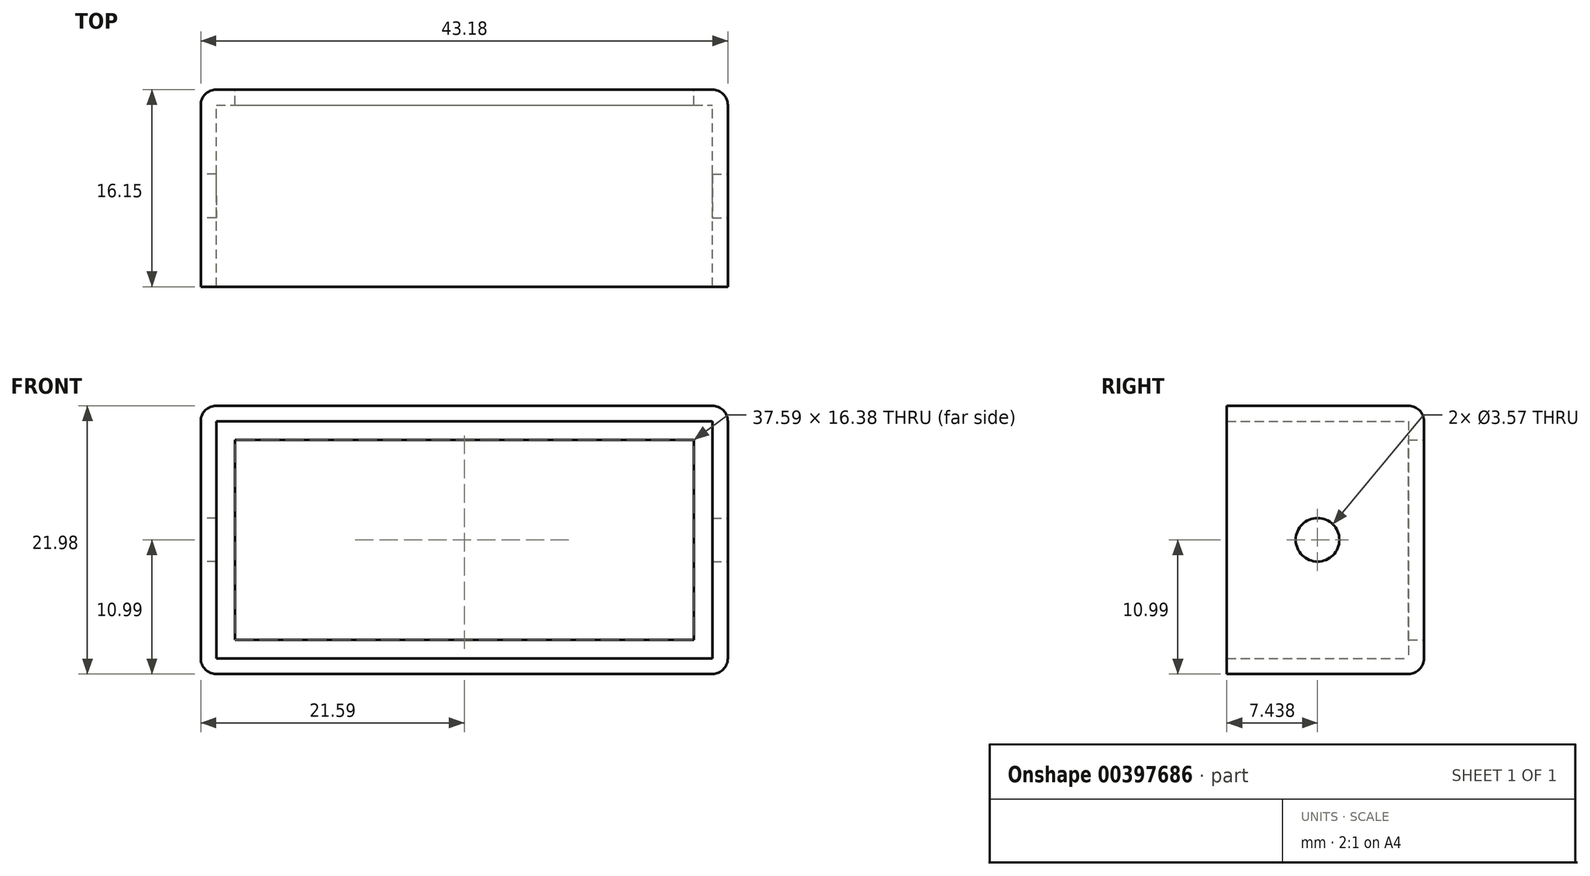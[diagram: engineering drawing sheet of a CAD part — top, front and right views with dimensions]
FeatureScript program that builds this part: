
annotation { "Feature Type Name" : "Feature", "Feature Type Description" : "" }
export const myFeature = defineFeature(function(context is Context, id is Id, definition is map)
    precondition{}
    {
        {
            var Q0;
            Q0=qCreatedBy(makeId("Front.planeOp"),FACE);
            var sketch = newSketch(context, id + "F0", { "sketchPlane" : qUnion([Q0])});
            skLineSegment(sketch, "E0.bottom", {"start": v(21.59, 10.99) * mm, "end": v(-21.59, 10.99) * mm});
            skLineSegment(sketch, "E0.top", {"start": v(21.59, -10.99) * mm, "end": v(-21.59, -10.99) * mm});
            skLineSegment(sketch, "E0.left", {"start": v(21.59, 10.99) * mm, "end": v(21.59, -10.99) * mm});
            skLineSegment(sketch, "E0.right", {"start": v(-21.59, 10.99) * mm, "end": v(-21.59, -10.99) * mm});
            skPoint(sketch, "E0.middle", {"position": v(0, 0) * mm});
            skLineSegment(sketch, "E1.bottom", {"start": v(-18.8, -8.2) * mm, "end": v(18.8, -8.2) * mm});
            skLineSegment(sketch, "E1.top", {"start": v(-18.8, 8.2) * mm, "end": v(18.8, 8.2) * mm});
            skLineSegment(sketch, "E1.left", {"start": v(-18.8, -8.2) * mm, "end": v(-18.8, 8.2) * mm});
            skLineSegment(sketch, "E1.right", {"start": v(18.8, -8.2) * mm, "end": v(18.8, 8.2) * mm});
            skLineSegment(sketch, "E2.bottom", {"start": v(-20.32, 9.72) * mm, "end": v(20.32, 9.72) * mm});
            skLineSegment(sketch, "E2.top", {"start": v(-20.32, -9.72) * mm, "end": v(20.32, -9.72) * mm});
            skLineSegment(sketch, "E2.left", {"start": v(-20.32, 9.72) * mm, "end": v(-20.32, -9.72) * mm});
            skLineSegment(sketch, "E2.right", {"start": v(20.32, 9.72) * mm, "end": v(20.32, -9.72) * mm});
            skSolve(sketch);
        }
        {
            var Q0;
            Q0=makeQuery(id+"F0.imprint","IMPRINT",FACE,{"disambiguationData":[TD([[makeQuery(id+"F0.imprint","IMPRINT",EDGE,{"derivedFrom":sQuery(id+"F0.wireOp",EDGE,"E0.bottom")}),1.0]])]});
            extrude(context, id + "F1", {"entities" : qUnion([Q0]), "depth" : 16.15 * mm});
        }
        {
            var Q0;
            Q0=makeQuery(id+"F0.imprint","IMPRINT",FACE,{"disambiguationData":[TD([[makeQuery(id+"F0.imprint","IMPRINT",EDGE,{"derivedFrom":sQuery(id+"F0.wireOp",EDGE,"E1.bottom")}),-1.0]])]});
            extrude(context, id + "F2", {"entities" : qUnion([Q0]), "operationType" : NewBodyOperationType.ADD, "depth" : 1.27 * mm});
        }
        {
            var Q0;
            Q0=makeQuery(id+"F1.opExtrude","SWEPT_EDGE",EDGE,{"disambiguationData":[OSD([sQuery(id+"F0.wireOp",EDGE,"E0.bottom"),sQuery(id+"F0.wireOp",EDGE,"E0.right")])]});
            var Q1;
            Q1=makeQuery(id+"F1.opExtrude","SWEPT_EDGE",EDGE,{"disambiguationData":[OSD([sQuery(id+"F0.wireOp",EDGE,"E0.top"),sQuery(id+"F0.wireOp",EDGE,"E0.right")])]});
            var Q2;
            Q2=makeQuery(id+"F1.opExtrude","SWEPT_EDGE",EDGE,{"disambiguationData":[OSD([sQuery(id+"F0.wireOp",EDGE,"E0.top"),sQuery(id+"F0.wireOp",EDGE,"E0.left")])]});
            var Q3;
            Q3=makeQuery(id+"F1.opExtrude","SWEPT_EDGE",EDGE,{"disambiguationData":[OSD([sQuery(id+"F0.wireOp",EDGE,"E0.bottom"),sQuery(id+"F0.wireOp",EDGE,"E0.left")])]});
            fillet(context, id + "F3", {"entities" : qUnion([Q0, Q1, Q2, Q3]), "radius" : 1.27 * mm, "tangentPropagation" : true, "allowEdgeOverflow" : false});
        }
        {
            var Q0;
            Q0=makeQuery(id+"F1.opExtrude","CAP_EDGE",EDGE,{"disambiguationData":[OSD([sQuery(id+"F0.wireOp",EDGE,"E0.top")])],"isStart":true});
            fillet(context, id + "F4", {"entities" : qUnion([Q0]), "radius" : 1.27 * mm, "tangentPropagation" : true, "allowEdgeOverflow" : false});
        }
        {
            var Q0;
            Q0=makeQuery(id+"F1.opExtrude","SWEPT_FACE",FACE,{"disambiguationData":[OSD([sQuery(id+"F0.wireOp",EDGE,"E0.left")])]});
            var sketch = newSketch(context, id + "F5", { "sketchPlane" : qUnion([Q0])});
            skLineSegment(sketch, "E3", {"start": v(-8.71, 9.72) * mm, "end": v(-8.71, -9.72) * mm, "construction": true});
            skLineSegment(sketch, "E4", {"start": v(-16.15, 0) * mm, "end": v(-1.27, 0) * mm, "construction": true});
            skCircle(sketch, "E5", {"center": v(-8.71, 0) * mm, "radius": 1.79 * mm});
            skSolve(sketch);
        }
        {
            var Q0;
            Q0=makeQuery(id+"F5.imprint","IMPRINT",FACE,{"disambiguationData":[TD([[makeQuery(id+"F5.imprint","IMPRINT",EDGE,{"derivedFrom":sQuery(id+"F5.wireOp",EDGE,"E5")}),1.0]])]});
            extrude(context, id + "F6", {"entities" : qUnion([Q0]), "operationType" : NewBodyOperationType.REMOVE, "oppositeDirection" : true, "depth" : 7.62 * mm});
        }
        {
            var Q0;
            Q0=makeQuery(id+"F1.opExtrude","SWEPT_FACE",FACE,{"disambiguationData":[OSD([sQuery(id+"F0.wireOp",EDGE,"E0.right")])]});
            var sketch = newSketch(context, id + "F7", { "sketchPlane" : qUnion([Q0])});
            skLineSegment(sketch, "E6", {"start": v(8.71, -9.72) * mm, "end": v(8.71, 9.72) * mm, "construction": true});
            skLineSegment(sketch, "E7", {"start": v(16.15, 0) * mm, "end": v(1.27, 0) * mm, "construction": true});
            skCircle(sketch, "E8", {"center": v(8.71, 0) * mm, "radius": 1.79 * mm});
            skSolve(sketch);
        }
        {
            var Q0;
            Q0=makeQuery(id+"F7.imprint","IMPRINT",FACE,{"disambiguationData":[TD([[makeQuery(id+"F7.imprint","IMPRINT",EDGE,{"derivedFrom":sQuery(id+"F7.wireOp",EDGE,"E8")}),1.0]])]});
            extrude(context, id + "F8", {"entities" : qUnion([Q0]), "operationType" : NewBodyOperationType.REMOVE, "oppositeDirection" : true, "depth" : 7.62 * mm});
        }
    });
